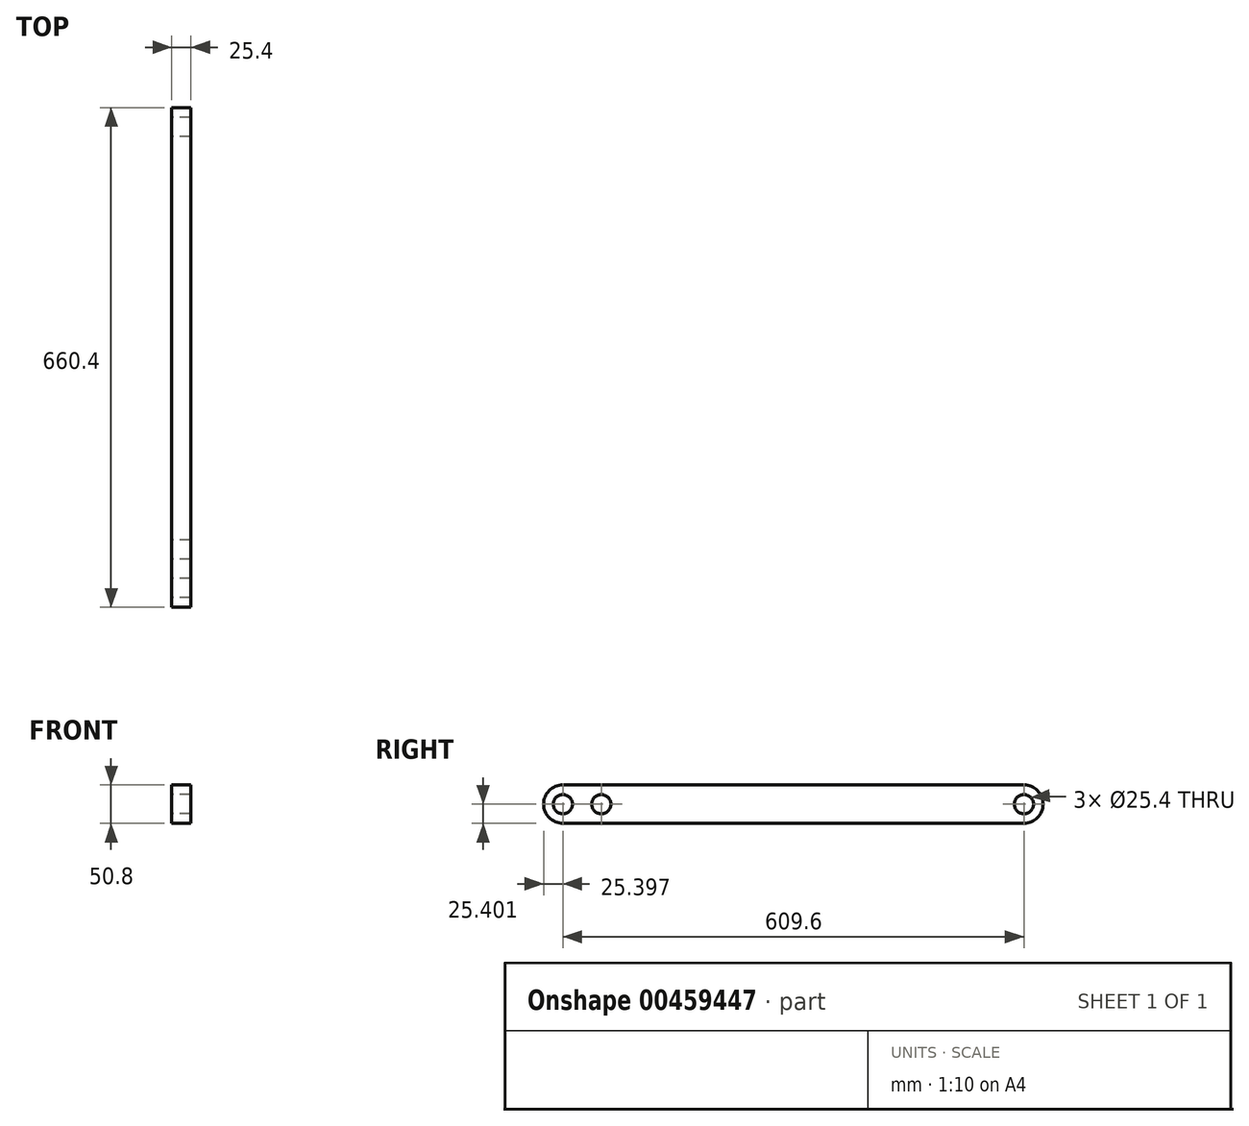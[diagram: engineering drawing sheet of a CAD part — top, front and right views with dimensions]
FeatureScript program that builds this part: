
annotation { "Feature Type Name" : "Feature", "Feature Type Description" : "" }
export const myFeature = defineFeature(function(context is Context, id is Id, definition is map)
    precondition{}
    {
        {
            var Q0;
            Q0=qCreatedBy(makeId("Right.planeOp"),FACE);
            var sketch = newSketch(context, id + "F0", { "sketchPlane" : qUnion([Q0])});
            skLineSegment(sketch, "E0.bottom", {"start": v(-265.08, 4.3) * mm, "end": v(344.52, 4.3) * mm});
            skLineSegment(sketch, "E0.top", {"start": v(-265.08, -46.5) * mm, "end": v(344.52, -46.5) * mm});
            skLineSegment(sketch, "E0.left", {"start": v(-265.08, 4.3) * mm, "end": v(-265.08, -46.5) * mm});
            skLineSegment(sketch, "E0.right", {"start": v(344.52, 4.3) * mm, "end": v(344.52, -46.5) * mm});
            skCircle(sketch, "E1", {"center": v(-265.08, -21.1) * mm, "radius": 25.4 * mm});
            skCircle(sketch, "E2", {"center": v(-265.08, -21.1) * mm, "radius": 12.7 * mm});
            skCircle(sketch, "E3", {"center": v(344.52, -21.1) * mm, "radius": 25.4 * mm});
            skCircle(sketch, "E4", {"center": v(344.52, -21.1) * mm, "radius": 12.7 * mm});
            skLineSegment(sketch, "E5", {"start": v(-239.68, -21.1) * mm, "end": v(-214.28, -21.1) * mm});
            skCircle(sketch, "E6", {"center": v(-214.28, -21.1) * mm, "radius": 12.7 * mm});
            skSolve(sketch);
        }
        {
            var Q0;
            Q0=qSketchRegion(id+"F0",true);
            extrude(context, id + "F1", {"entities" : qUnion([Q0]), "depth" : 25.4 * mm});
        }
    });
